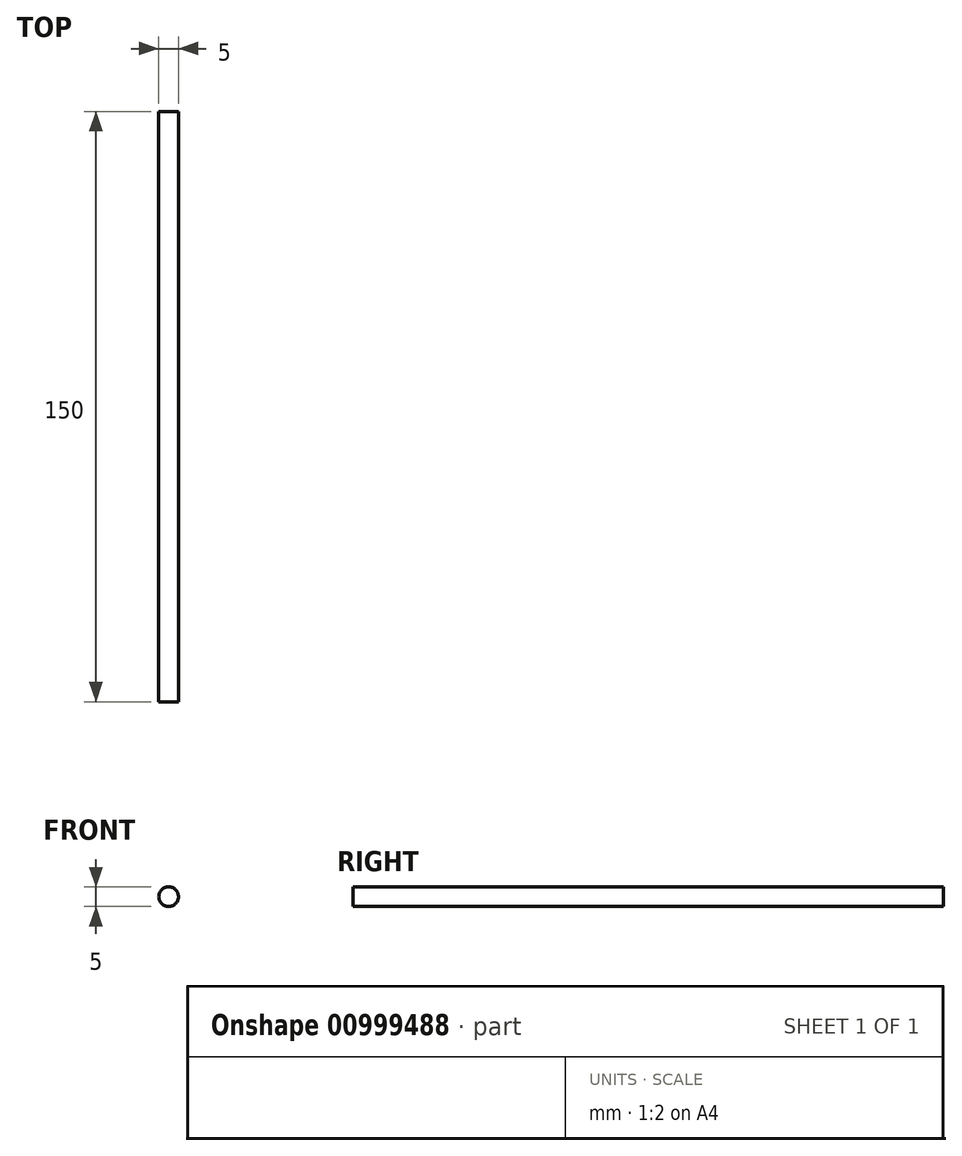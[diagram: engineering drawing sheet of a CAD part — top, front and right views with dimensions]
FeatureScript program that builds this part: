
annotation { "Feature Type Name" : "Feature", "Feature Type Description" : "" }
export const myFeature = defineFeature(function(context is Context, id is Id, definition is map)
    precondition{}
    {
        {
            var Q0;
            Q0=qCreatedBy(makeId("Front.planeOp"),FACE);
            var sketch = newSketch(context, id + "F0", { "sketchPlane" : qUnion([Q0])});
            skCircle(sketch, "E0", {"center": v(0, 0) * mm, "radius": 2.5 * mm});
            skSolve(sketch);
        }
        {
            var Q0;
            Q0 = qSketchRegion(id + "F0", true);
            extrude(context, id + "F1", {"entities" : qUnion([Q0]), "depth" : 150 * mm, "offsetDistance" : 25 * mm});
        }
    });
